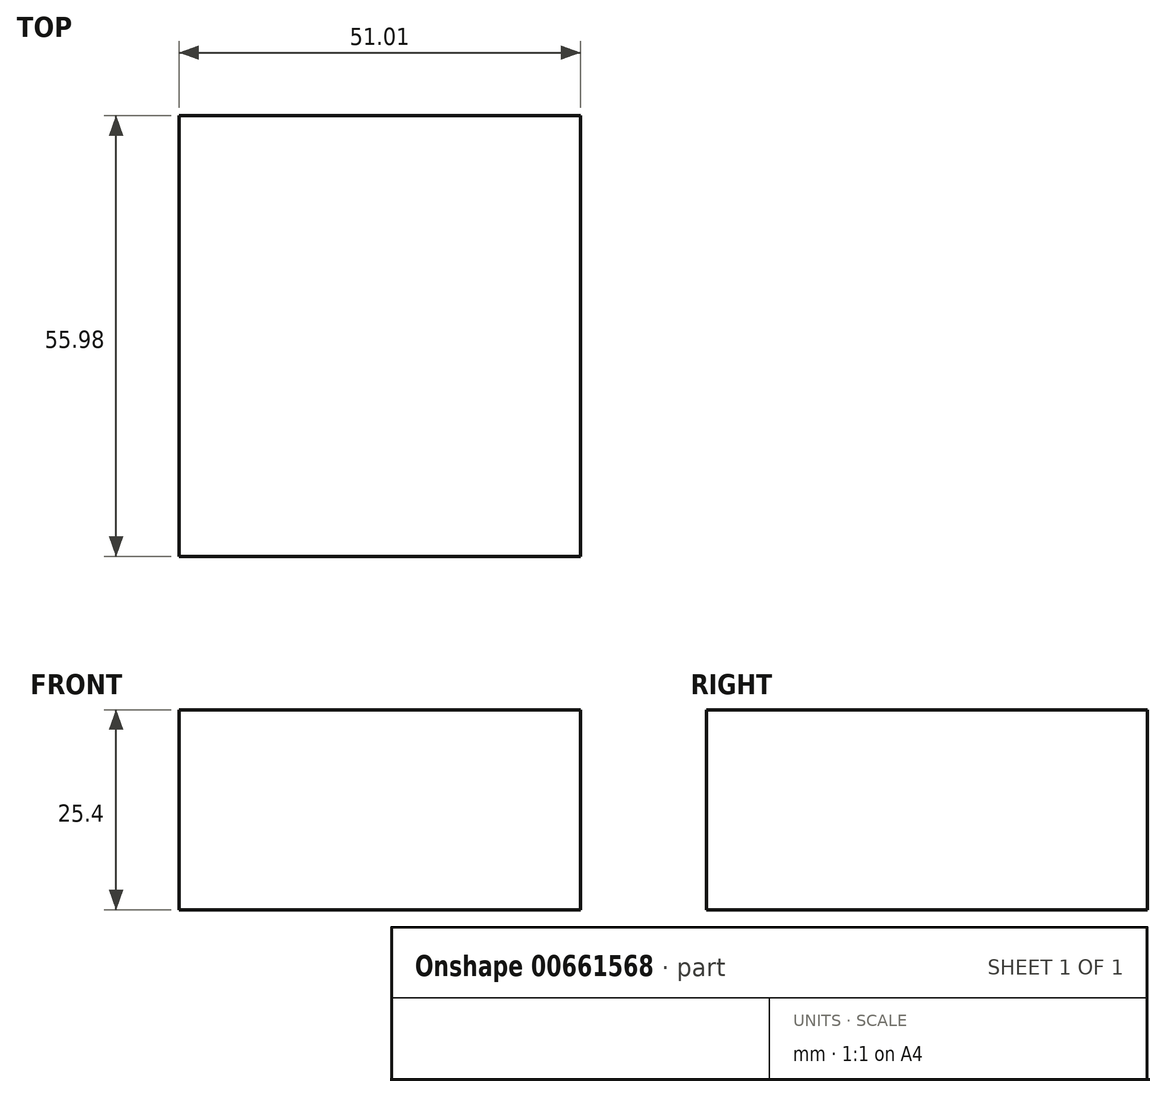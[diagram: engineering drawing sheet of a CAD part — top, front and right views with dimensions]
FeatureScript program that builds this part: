
annotation { "Feature Type Name" : "Feature", "Feature Type Description" : "" }
export const myFeature = defineFeature(function(context is Context, id is Id, definition is map)
    precondition{}
    {
        {
            var Q0;
            Q0=qCreatedBy(makeId("Top.planeOp"),FACE);
            var sketch = newSketch(context, id + "F0", { "sketchPlane" : qUnion([Q0])});
            skLineSegment(sketch, "E0.bottom", {"start": v(0, 55.98) * mm, "end": v(51.01, 55.98) * mm});
            skLineSegment(sketch, "E0.top", {"start": v(0, 0) * mm, "end": v(51.01, 0) * mm});
            skLineSegment(sketch, "E0.left", {"start": v(0, 55.98) * mm, "end": v(0, 0) * mm});
            skLineSegment(sketch, "E0.right", {"start": v(51.01, 55.98) * mm, "end": v(51.01, 0) * mm});
            skSolve(sketch);
        }
        {
            var Q0;
            Q0 = qSketchRegion(id + "F0", true);
            extrude(context, id + "F1", {"entities" : qUnion([Q0]), "depth" : 25.4 * mm, "offsetDistance" : 25.4 * mm});
        }
    });
